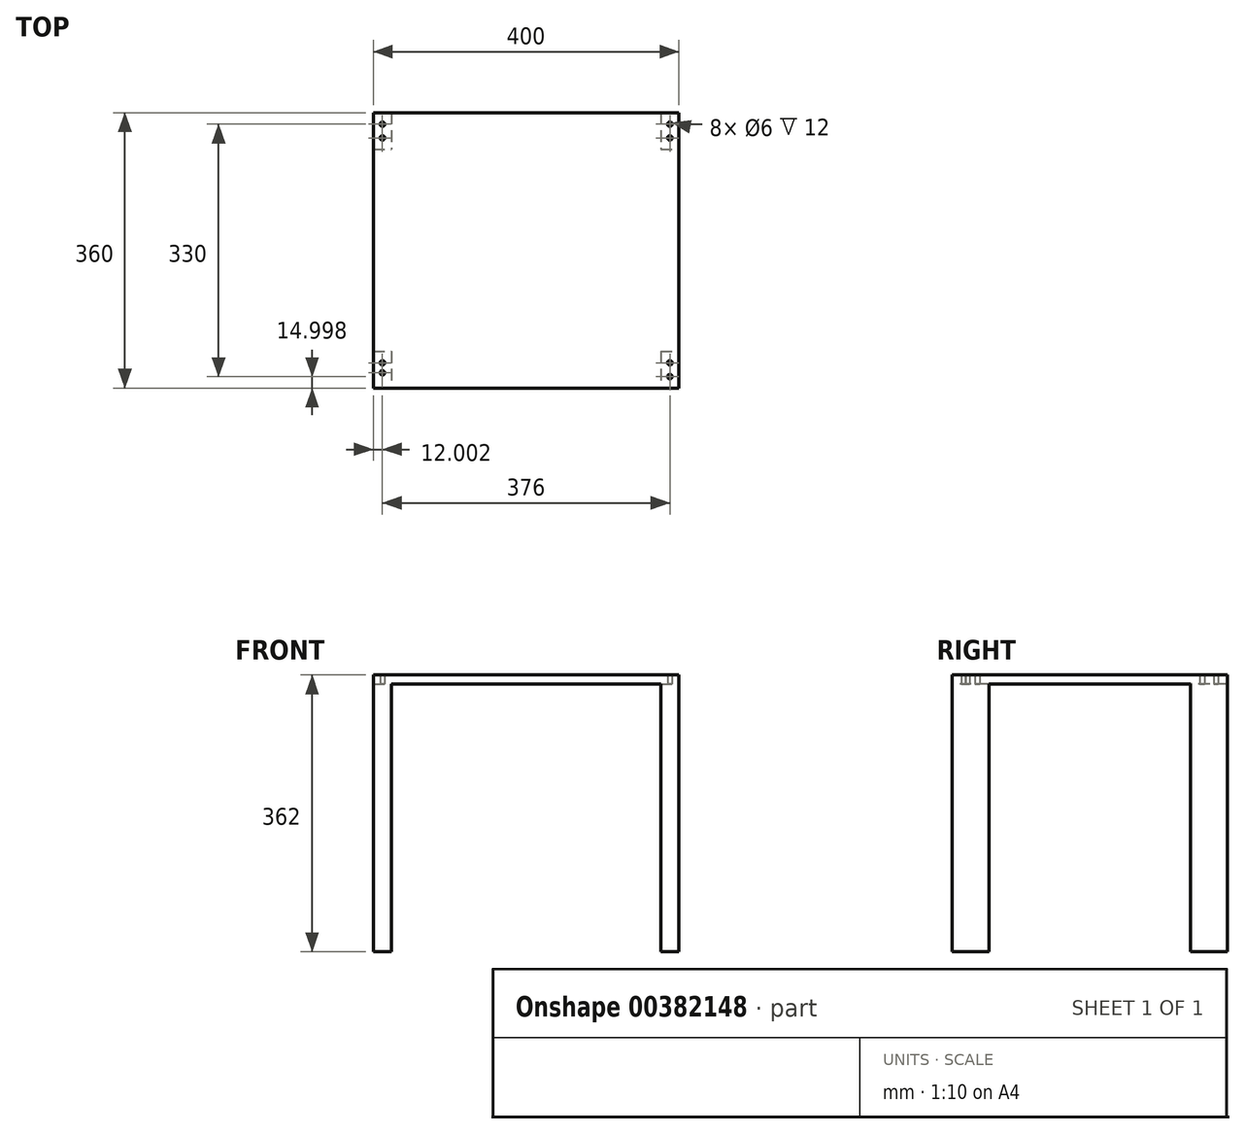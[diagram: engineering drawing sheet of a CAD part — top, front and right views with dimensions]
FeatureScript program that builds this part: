
annotation { "Feature Type Name" : "Feature", "Feature Type Description" : "" }
export const myFeature = defineFeature(function(context is Context, id is Id, definition is map)
    precondition{}
    {
        {
            var Q0;
            Q0=qCreatedBy(makeId("Top.planeOp"),FACE);
            var sketch = newSketch(context, id + "F0", { "sketchPlane" : qUnion([Q0])});
            skLineSegment(sketch, "E0.bottom", {"start": v(-230.97, 131.75) * mm, "end": v(169.03, 131.75) * mm});
            skLineSegment(sketch, "E0.top", {"start": v(-230.97, -228.25) * mm, "end": v(169.03, -228.25) * mm});
            skLineSegment(sketch, "E0.left", {"start": v(-230.97, 131.75) * mm, "end": v(-230.97, -228.25) * mm});
            skLineSegment(sketch, "E0.right", {"start": v(169.03, 131.75) * mm, "end": v(169.03, -228.25) * mm});
            skCircle(sketch, "E1", {"center": v(-218.97, -208.25) * mm, "radius": 3 * mm});
            skCircle(sketch, "E2", {"center": v(-218.97, -195.25) * mm, "radius": 3 * mm});
            skCircle(sketch, "E3", {"center": v(157.03, -213.25) * mm, "radius": 3 * mm});
            skCircle(sketch, "E4", {"center": v(157.03, -195.25) * mm, "radius": 3 * mm});
            skCircle(sketch, "E5", {"center": v(157.03, 98.75) * mm, "radius": 3 * mm});
            skCircle(sketch, "E6", {"center": v(157.03, 116.75) * mm, "radius": 3 * mm});
            skCircle(sketch, "E7", {"center": v(-218.97, 98.75) * mm, "radius": 3 * mm});
            skCircle(sketch, "E8", {"center": v(-218.97, 116.75) * mm, "radius": 3 * mm});
            skSolve(sketch);
        }
        {
            var Q0;
            Q0=qCreatedBy(makeId("Top.planeOp"),FACE);
            var sketch = newSketch(context, id + "F1", { "sketchPlane" : qUnion([Q0])});
            skLineSegment(sketch, "E9.bottom", {"start": v(-230.97, -180.25) * mm, "end": v(-206.97, -180.25) * mm});
            skLineSegment(sketch, "E9.top", {"start": v(-230.97, -228.25) * mm, "end": v(-206.97, -228.25) * mm});
            skLineSegment(sketch, "E9.left", {"start": v(-230.97, -180.25) * mm, "end": v(-230.97, -228.25) * mm});
            skLineSegment(sketch, "E9.right", {"start": v(-206.97, -180.25) * mm, "end": v(-206.97, -228.25) * mm});
            skLineSegment(sketch, "E10.bottom", {"start": v(-230.97, 131.75) * mm, "end": v(-206.97, 131.75) * mm});
            skLineSegment(sketch, "E10.top", {"start": v(-230.97, 83.75) * mm, "end": v(-206.97, 83.75) * mm});
            skLineSegment(sketch, "E10.left", {"start": v(-230.97, 131.75) * mm, "end": v(-230.97, 83.75) * mm});
            skLineSegment(sketch, "E10.right", {"start": v(-206.97, 131.75) * mm, "end": v(-206.97, 83.75) * mm});
            skLineSegment(sketch, "E11.bottom", {"start": v(145.03, 131.75) * mm, "end": v(169.03, 131.75) * mm});
            skLineSegment(sketch, "E11.top", {"start": v(145.03, 83.75) * mm, "end": v(169.03, 83.75) * mm});
            skLineSegment(sketch, "E11.left", {"start": v(145.03, 131.75) * mm, "end": v(145.03, 83.75) * mm});
            skLineSegment(sketch, "E11.right", {"start": v(169.03, 131.75) * mm, "end": v(169.03, 83.75) * mm});
            skLineSegment(sketch, "E12.bottom", {"start": v(145.03, -180.25) * mm, "end": v(169.03, -180.25) * mm});
            skLineSegment(sketch, "E12.top", {"start": v(145.03, -228.25) * mm, "end": v(169.03, -228.25) * mm});
            skLineSegment(sketch, "E12.left", {"start": v(145.03, -180.25) * mm, "end": v(145.03, -228.25) * mm});
            skLineSegment(sketch, "E12.right", {"start": v(169.03, -180.25) * mm, "end": v(169.03, -228.25) * mm});
            skSolve(sketch);
        }
        {
            var Q0;
            Q0 = qSketchRegion(id + "F0", true);
            extrude(context, id + "F2", {"entities" : qUnion([Q0]), "depth" : 12 * mm});
        }
        {
            var Q0;
            Q0 = qSketchRegion(id + "F1", true);
            extrude(context, id + "F3", {"entities" : qUnion([Q0]), "operationType" : NewBodyOperationType.ADD, "depth" : -350 * mm});
        }
    });
